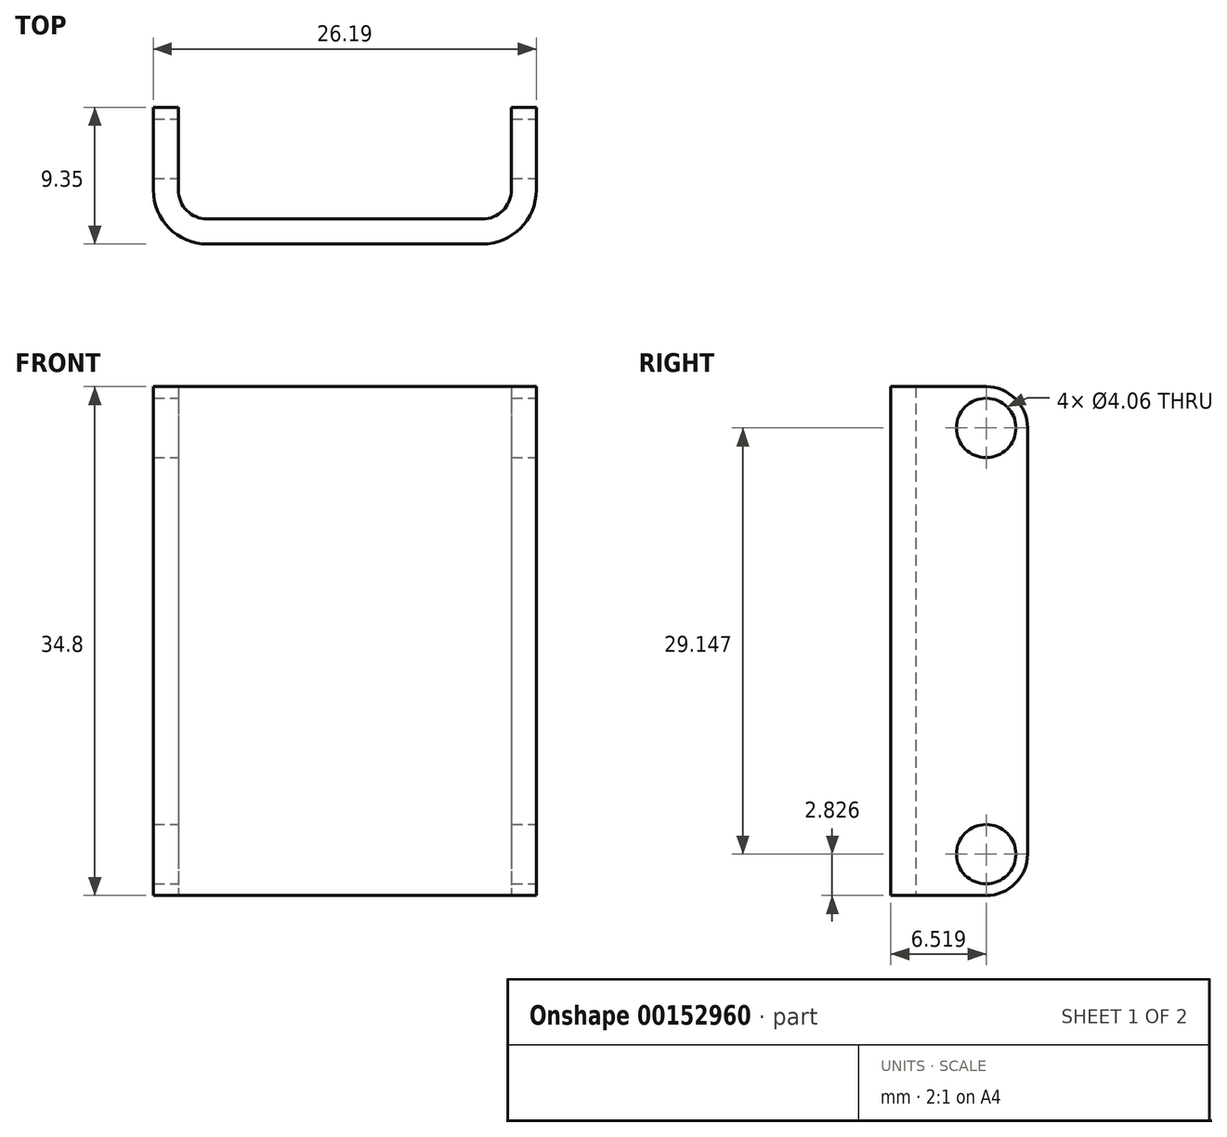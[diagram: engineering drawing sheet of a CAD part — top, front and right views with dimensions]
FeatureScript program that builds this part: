
annotation { "Feature Type Name" : "Feature", "Feature Type Description" : "" }
export const myFeature = defineFeature(function(context is Context, id is Id, definition is map)
    precondition{}
    {
        {
            var Q0;
            Q0=qCreatedBy(makeId("Top.planeOp"),FACE);
            var sketch = newSketch(context, id + "F0", { "sketchPlane" : qUnion([Q0])});
            skLineSegment(sketch, "E0.bottom", {"start": v(0, 0) * mm, "end": v(-22.77, 0) * mm});
            skLineSegment(sketch, "E0.top", {"start": v(1.7, -1.7) * mm, "end": v(-24.48, -1.7) * mm});
            skLineSegment(sketch, "E1.top", {"start": v(-22.77, 7.64) * mm, "end": v(-24.48, 7.64) * mm});
            skLineSegment(sketch, "E1.left", {"start": v(-22.77, 0) * mm, "end": v(-22.77, 7.64) * mm});
            skLineSegment(sketch, "E1.right", {"start": v(-24.48, -1.7) * mm, "end": v(-24.48, 7.64) * mm});
            skLineSegment(sketch, "E2.top", {"start": v(0, 7.64) * mm, "end": v(1.7, 7.64) * mm});
            skLineSegment(sketch, "E2.left", {"start": v(0, 0) * mm, "end": v(0, 7.64) * mm});
            skLineSegment(sketch, "E2.right", {"start": v(1.7, -1.7) * mm, "end": v(1.7, 7.64) * mm});
            skLineSegment(sketch, "E3", {"start": v(-11.38, 0) * mm, "end": v(-11.38, -1.7) * mm, "construction": true});
            skArc(sketch, "E4", {"start": v(-1.98, 0) * mm, "mid": v(-0.58, 0.58) * mm, "end": v(0, 1.98) * mm, "construction": true});
            skSolve(sketch);
        }
        {
            var Q0;
            Q0=qSketchRegion(id+"F0",true);
            extrude(context, id + "F1", {"entities" : qUnion([Q0]), "depth" : 34.8 * mm});
        }
        {
            var Q0;
            Q0=makeQuery(id+"F1.opExtrude","SWEPT_EDGE",EDGE,{"disambiguationData":[OSD([sQuery(id+"F0.wireOp",EDGE,"E0.top"),sQuery(id+"F0.wireOp",EDGE,"E2.right")])]});
            var Q1;
            Q1=makeQuery(id+"F1.opExtrude","SWEPT_EDGE",EDGE,{"disambiguationData":[OSD([sQuery(id+"F0.wireOp",EDGE,"E0.top"),sQuery(id+"F0.wireOp",EDGE,"E1.right")])]});
            var Q2;
            Q2=makeQuery(id+"FqNnmMD7oaRdpTN_1.opExtrude","CAP_EDGE",EDGE,{"disambiguationData":[OSD([sQuery(id+"FY5sMr6MULj5lJw_1.wireOp",EDGE,"W42EfhJi-fDm4-L9BW-folL-irsYfDskuzBk.top")])],"isStart":false});
            fillet(context, id + "F2", {"entities" : qUnion([Q0, Q1, Q2]), "radius" : 3.7 * mm, "tangentPropagation" : true, "allowEdgeOverflow" : false});
        }
        {
            var Q0;
            Q0=makeQuery(id+"F1.opExtrude","SWEPT_EDGE",EDGE,{"disambiguationData":[OSD([sQuery(id+"F0.wireOp",EDGE,"E0.bottom"),sQuery(id+"F0.wireOp",EDGE,"E2.left")])]});
            var Q1;
            Q1=makeQuery(id+"F1.opExtrude","SWEPT_EDGE",EDGE,{"disambiguationData":[OSD([sQuery(id+"F0.wireOp",EDGE,"E0.bottom"),sQuery(id+"F0.wireOp",EDGE,"E1.left")])]});
            fillet(context, id + "F3", {"entities" : qUnion([Q0, Q1]), "radius" : 1.98 * mm, "tangentPropagation" : true, "allowEdgeOverflow" : false});
        }
        {
            var Q0;
            Q0=makeQuery(id+"F1.opExtrude","SWEPT_FACE",FACE,{"disambiguationData":[OSD([sQuery(id+"F0.wireOp",EDGE,"E2.right")])]});
            var sketch = newSketch(context, id + "F4", { "sketchPlane" : qUnion([Q0])});
            skLineSegment(sketch, "E5.bottom", {"start": v(4.8, 0) * mm, "end": v(7.64, 0) * mm, "construction": true});
            skLineSegment(sketch, "E5.top", {"start": v(4.8, 2.83) * mm, "end": v(7.64, 2.83) * mm, "construction": true});
            skLineSegment(sketch, "E5.left", {"start": v(4.8, 0) * mm, "end": v(4.8, 2.83) * mm, "construction": true});
            skLineSegment(sketch, "E5.right", {"start": v(7.64, 0) * mm, "end": v(7.64, 2.83) * mm, "construction": true});
            skLineSegment(sketch, "E6.bottom", {"start": v(4.8, 34.8) * mm, "end": v(7.64, 34.8) * mm, "construction": true});
            skLineSegment(sketch, "E6.top", {"start": v(4.8, 31.97) * mm, "end": v(7.64, 31.97) * mm, "construction": true});
            skLineSegment(sketch, "E6.left", {"start": v(4.8, 34.8) * mm, "end": v(4.8, 31.97) * mm, "construction": true});
            skLineSegment(sketch, "E6.right", {"start": v(7.64, 34.8) * mm, "end": v(7.64, 31.97) * mm, "construction": true});
            skCircle(sketch, "E7", {"center": v(4.8, 2.83) * mm, "radius": 2.03 * mm});
            skCircle(sketch, "E8", {"center": v(4.8, 31.97) * mm, "radius": 2.03 * mm});
            skSolve(sketch);
        }
        {
            var Q0;
            Q0=qSketchRegion(id+"F4",true);
            var Q1;
            Q1=makeQuery(id+"F1.opExtrude","SWEPT_FACE",FACE,{"disambiguationData":[OSD([sQuery(id+"F0.wireOp",EDGE,"E1.right")])]});
            extrude(context, id + "F5", {"entities" : qUnion([Q0]), "operationType" : NewBodyOperationType.REMOVE, "endBound" : BoundingType.UP_TO_SURFACE, "oppositeDirection" : true, "endBoundEntityFace" : qUnion([Q1]), "depth" : 25.4 * mm});
        }
        {
            var Q0;
            Q0=makeQuery(id+"F1.opExtrude","CAP_EDGE",EDGE,{"disambiguationData":[OSD([sQuery(id+"F0.wireOp",EDGE,"E2.top")])],"isStart":false});
            var Q1;
            Q1=makeQuery(id+"F1.opExtrude","CAP_EDGE",EDGE,{"disambiguationData":[OSD([sQuery(id+"F0.wireOp",EDGE,"E1.top")])],"isStart":false});
            var Q2;
            Q2=makeQuery(id+"F1.opExtrude","CAP_EDGE",EDGE,{"disambiguationData":[OSD([sQuery(id+"F0.wireOp",EDGE,"E2.top")])],"isStart":true});
            var Q3;
            Q3=makeQuery(id+"F1.opExtrude","CAP_EDGE",EDGE,{"disambiguationData":[OSD([sQuery(id+"F0.wireOp",EDGE,"E1.top")])],"isStart":true});
            fillet(context, id + "F6", {"entities" : qUnion([Q0, Q1, Q2, Q3]), "radius" : 2.83 * mm, "tangentPropagation" : true, "allowEdgeOverflow" : false});
        }
    });
